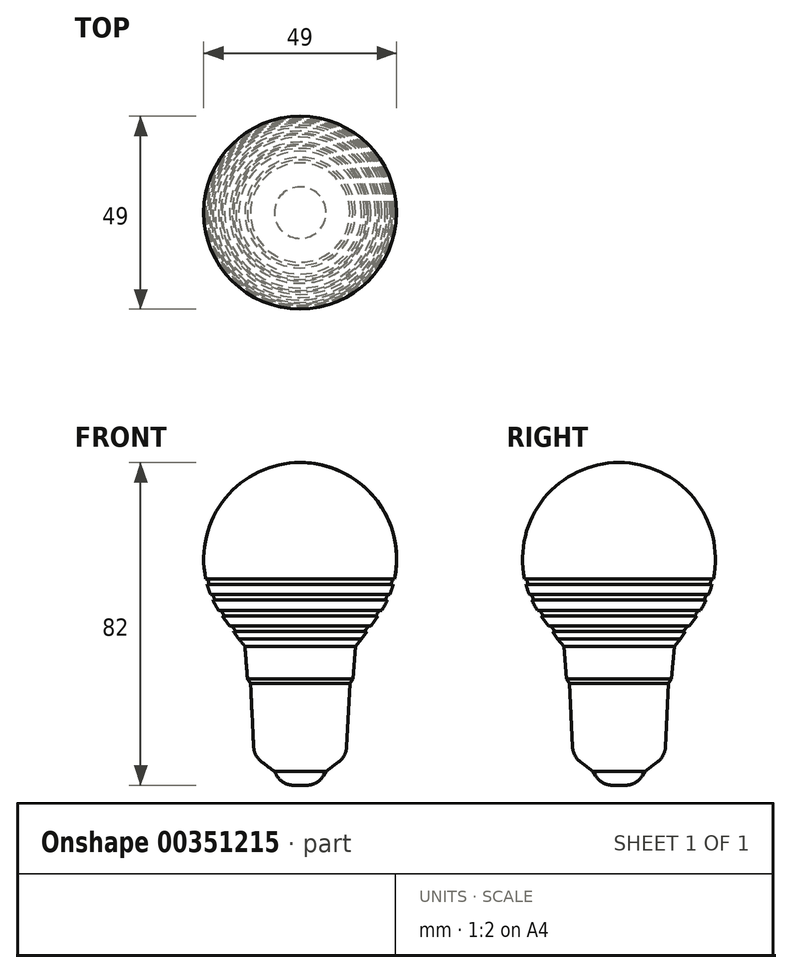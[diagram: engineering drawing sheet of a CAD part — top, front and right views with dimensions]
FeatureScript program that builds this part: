
annotation { "Feature Type Name" : "Feature", "Feature Type Description" : "" }
export const myFeature = defineFeature(function(context is Context, id is Id, definition is map)
    precondition{}
    {
        {
            var Q0;
            Q0=qCreatedBy(makeId("Front.planeOp"),FACE);
            var sketch = newSketch(context, id + "F0", { "sketchPlane" : qUnion([Q0])});
            skLineSegment(sketch, "E0", {"start": v(0, 0) * mm, "end": v(0, 91.65) * mm});
            skArc(sketch, "E1", {"start": v(0, 82) * mm, "mid": v(19.02, 72.95) * mm, "end": v(23.98, 52.47) * mm});
            skLineSegment(sketch, "E2", {"start": v(14.04, 35.31) * mm, "end": v(13.38, 27.03) * mm});
            skLineSegment(sketch, "E3", {"start": v(13.38, 27.03) * mm, "end": v(12.62, 25.9) * mm});
            skLineSegment(sketch, "E4", {"start": v(6.55, 3.55) * mm, "end": v(9.8, 5.98) * mm});
            skLineSegment(sketch, "E5", {"start": v(6.55, 3.55) * mm, "end": v(5.96, 2.52) * mm});
            skLineSegment(sketch, "E6", {"start": v(1.62, 0) * mm, "end": v(0, 0) * mm});
            skLineSegment(sketch, "E7", {"start": v(11.8, 9.73) * mm, "end": v(12.62, 25.9) * mm});
            skPoint(sketch, "E8.0.internal.orphan", {"position": v(24.5, 57.5) * mm});
            skLineSegment(sketch, "E9", {"start": v(14.04, 35.31) * mm, "end": v(15.6, 37.21) * mm});
            skLineSegment(sketch, "E10", {"start": v(15.6, 37.21) * mm, "end": v(16.94, 39.07) * mm});
            skLineSegment(sketch, "E11.bottom", {"start": v(23.98, 52.47) * mm, "end": v(23.47, 52.47) * mm});
            skLineSegment(sketch, "E11.top", {"start": v(23.64, 51.07) * mm, "end": v(23.12, 51.07) * mm});
            skLineSegment(sketch, "E12.0.1.1", {"start": v(22.78, 48.47) * mm, "end": v(22.24, 48.47) * mm});
            skLineSegment(sketch, "E12.0.1.2", {"start": v(22.17, 47.07) * mm, "end": v(21.62, 47.07) * mm});
            skLineSegment(sketch, "E12.0.2.1", {"start": v(20.75, 44.47) * mm, "end": v(20.16, 44.47) * mm});
            skLineSegment(sketch, "E12.0.2.2", {"start": v(19.8, 43.07) * mm, "end": v(19.18, 43.07) * mm});
            skLineSegment(sketch, "E12.0.3.1", {"start": v(17.94, 40.47) * mm, "end": v(17.33, 40.47) * mm});
            skLineSegment(sketch, "E12.0.3.2", {"start": v(16.94, 39.07) * mm, "end": v(16.32, 39.07) * mm});
            skLineSegment(sketch, "E12.direction1", {"start": v(23.12, 51.07) * mm, "end": v(23.64, 51.07) * mm, "construction": true});
            skArc(sketch, "E13.0", {"start": v(23.47, 52.47) * mm, "mid": v(23.3, 51.77) * mm, "end": v(23.12, 51.07) * mm});
            skLineSegment(sketch, "E14.0", {"start": v(16.32, 39.07) * mm, "end": v(17.33, 40.47) * mm});
            skLineSegment(sketch, "E15.trimOffspring", {"start": v(17.94, 40.47) * mm, "end": v(19.8, 43.07) * mm});
            skArc(sketch, "E16.trimOffspring", {"start": v(22.17, 47.07) * mm, "mid": v(21.5, 45.75) * mm, "end": v(20.75, 44.47) * mm});
            skArc(sketch, "E17.trimOffspring", {"start": v(20.16, 44.47) * mm, "mid": v(19.68, 43.77) * mm, "end": v(19.18, 43.07) * mm});
            skArc(sketch, "E18.trimOffspring", {"start": v(22.24, 48.47) * mm, "mid": v(21.94, 47.77) * mm, "end": v(21.62, 47.07) * mm});
            skArc(sketch, "E19.trimOffspring", {"start": v(23.64, 51.07) * mm, "mid": v(23.25, 49.76) * mm, "end": v(22.78, 48.47) * mm});
            skPoint(sketch, "E20.visualSharp", {"position": v(11.68, 7.39) * mm});
            skArc(sketch, "E20.filletArc", {"start": v(9.8, 5.98) * mm, "mid": v(11.22, 7.63) * mm, "end": v(11.8, 9.73) * mm});
            skPoint(sketch, "E21.visualSharp", {"position": v(4.52, 0) * mm});
            skArc(sketch, "E21.filletArc", {"start": v(1.62, 0) * mm, "mid": v(4.13, 0.67) * mm, "end": v(5.96, 2.52) * mm});
            skSolve(sketch);
        }
        {
            var Q0;
            Q0 = qSketchRegion(id + "F0", true);
            var Q1;
            Q1=sQuery(id+"F0.wireOp",EDGE,"E0");
            revolve(context, id + "F1", {"entities" : qUnion([Q0]), "axis" : qUnion([Q1]), "revolveType" : RevolveType.FULL});
        }
    });
